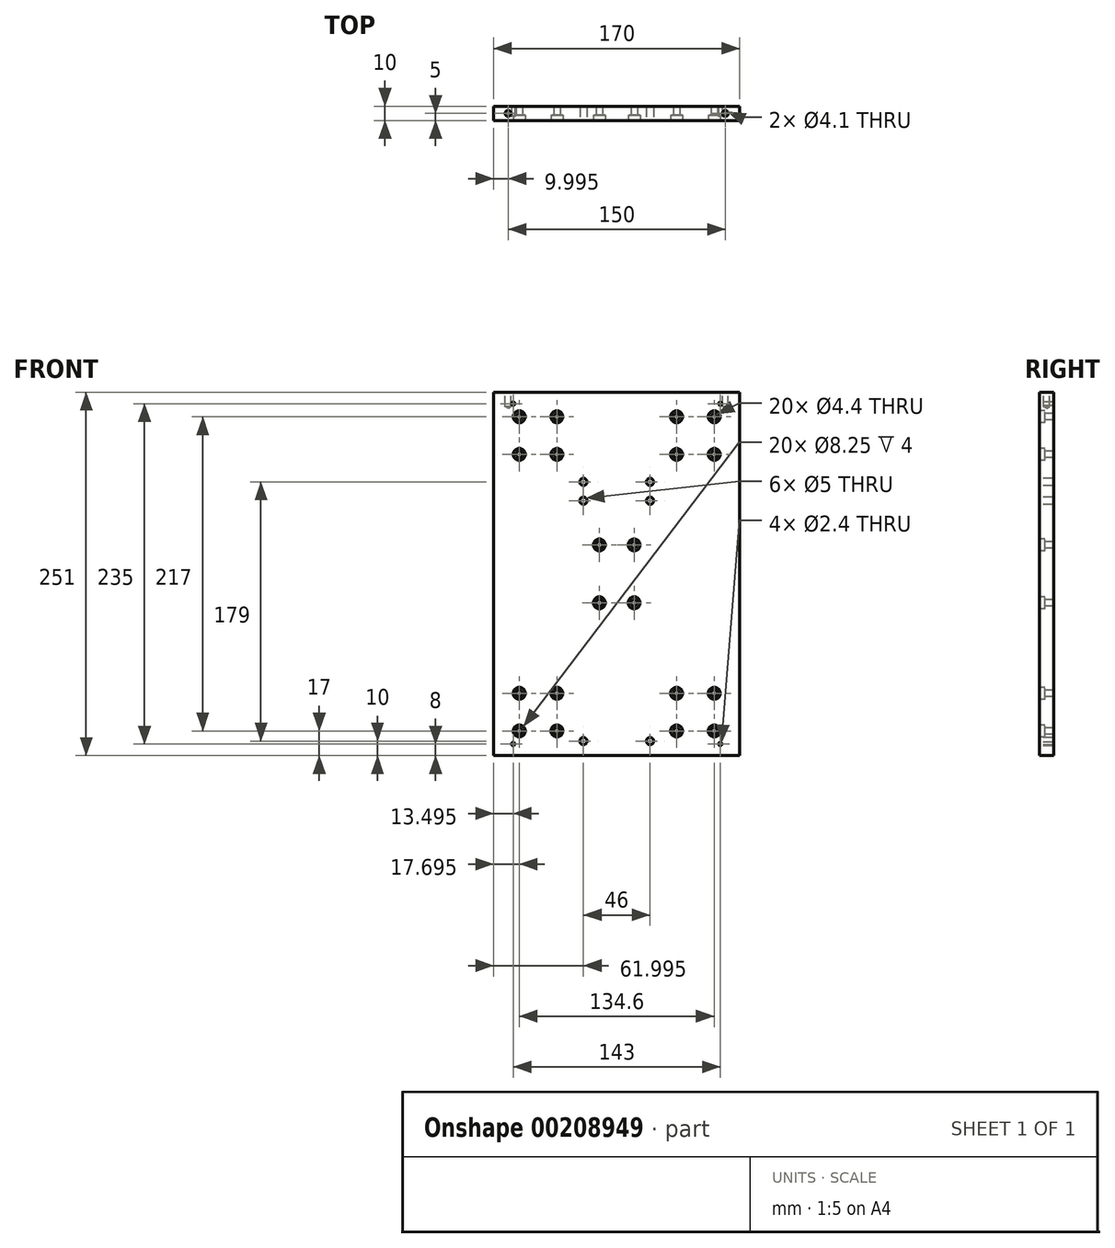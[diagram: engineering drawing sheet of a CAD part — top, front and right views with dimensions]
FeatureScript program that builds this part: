
annotation { "Feature Type Name" : "Feature", "Feature Type Description" : "" }
export const myFeature = defineFeature(function(context is Context, id is Id, definition is map)
    precondition{}
    {
        {
            var Q0;
            Q0=qCreatedBy(makeId("Front.planeOp"),FACE);
            var sketch = newSketch(context, id + "F0", { "sketchPlane" : qUnion([Q0])});
            skLineSegment(sketch, "E0.bottom", {"start": v(-43.58, 205.06) * mm, "end": v(126.42, 205.06) * mm});
            skLineSegment(sketch, "E0.top", {"start": v(-43.58, -40.94) * mm, "end": v(126.42, -40.94) * mm});
            skLineSegment(sketch, "E0.left", {"start": v(-43.58, 205.06) * mm, "end": v(-43.58, -40.94) * mm});
            skLineSegment(sketch, "E0.right", {"start": v(126.42, 205.06) * mm, "end": v(126.42, -40.94) * mm});
            skSolve(sketch);
        }
        {
            var Q0;
            Q0=makeQuery(id+"F0.imprint","IMPRINT",FACE,{"disambiguationData":[TD([[makeQuery(id+"F0.imprint","IMPRINT",EDGE,{"derivedFrom":sQuery(id+"F0.wireOp",EDGE,"E0.bottom")}),-1.0]])]});
            extrude(context, id + "F1", {"entities" : qUnion([Q0]), "depth" : 10 * mm});
        }
        {
            var Q0;
            Q0=makeQuery(id+"F1.opExtrude","CAP_FACE",FACE,{"disambiguationData":[OSD([sQuery(id+"F0.wireOp",EDGE,"E0.bottom"),sQuery(id+"F0.wireOp",EDGE,"E0.top"),sQuery(id+"F0.wireOp",EDGE,"E0.left"),sQuery(id+"F0.wireOp",EDGE,"E0.right")])],"isStart":false});
            var sketch = newSketch(context, id + "F2", { "sketchPlane" : qUnion([Q0])});
            skLineSegment(sketch, "E1", {"start": v(41.42, 205.06) * mm, "end": v(41.42, -40.94) * mm, "construction": true});
            skLineSegment(sketch, "E2", {"start": v(-30.08, 205.06) * mm, "end": v(-30.08, -40.94) * mm, "construction": true});
            skLineSegment(sketch, "E3.MirrorCS", {"start": v(112.92, 205.06) * mm, "end": v(112.92, -40.94) * mm, "construction": true});
            skLineSegment(sketch, "E4", {"start": v(112.92, 202.06) * mm, "end": v(-30.08, 202.06) * mm, "construction": true});
            skLineSegment(sketch, "E5", {"start": v(112.92, -32.94) * mm, "end": v(-30.08, -32.94) * mm, "construction": true});
            skPoint(sketch, "E6", {"position": v(112.92, 202.06) * mm});
            skPoint(sketch, "E7", {"position": v(-30.08, 202.06) * mm});
            skPoint(sketch, "E8", {"position": v(112.92, -32.94) * mm});
            skPoint(sketch, "E9", {"position": v(-30.08, -32.94) * mm});
            skPoint(sketch, "E10", {"position": v(18.42, -30.94) * mm});
            skPoint(sketch, "E11.MirrorP", {"position": v(64.42, -30.94) * mm});
            skLineSegment(sketch, "E12", {"start": v(112.92, 148.06) * mm, "end": v(-30.08, 148.06) * mm, "construction": true});
            skLineSegment(sketch, "E13", {"start": v(112.92, 135.06) * mm, "end": v(-30.08, 135.06) * mm, "construction": true});
            skPoint(sketch, "E14", {"position": v(64.42, 148.06) * mm});
            skPoint(sketch, "E15.MirrorP", {"position": v(18.42, 148.06) * mm});
            skPoint(sketch, "E16", {"position": v(64.42, 135.06) * mm});
            skPoint(sketch, "E17.MirrorP", {"position": v(18.42, 135.06) * mm});
            skLineSegment(sketch, "E18", {"start": v(41.42, 219.06) * mm, "end": v(11.42, 219.06) * mm, "construction": true});
            skLineSegment(sketch, "E19", {"start": v(11.42, 219.06) * mm, "end": v(11.42, 244.06) * mm, "construction": true});
            skLineSegment(sketch, "E20", {"start": v(11.42, 244.06) * mm, "end": v(41.42, 244.06) * mm, "construction": true});
            skLineSegment(sketch, "E21", {"start": v(-43.58, -10.94) * mm, "end": v(126.42, -10.94) * mm, "construction": true});
            skLineSegment(sketch, "E22", {"start": v(-43.58, 180.06) * mm, "end": v(126.42, 180.06) * mm, "construction": true});
            skPoint(sketch, "E23", {"position": v(-25.88, 2.06) * mm});
            skPoint(sketch, "E24.MirrorP", {"position": v(-25.88, -23.94) * mm});
            skPoint(sketch, "E25.MirrorP", {"position": v(108.72, 2.06) * mm});
            skPoint(sketch, "E26.MirrorP", {"position": v(108.72, -23.94) * mm});
            skPoint(sketch, "E27", {"position": v(0.12, 2.06) * mm});
            skPoint(sketch, "E28.MirrorP", {"position": v(82.72, 2.06) * mm});
            skPoint(sketch, "E29.MirrorP", {"position": v(0.12, -23.94) * mm});
            skPoint(sketch, "E30.MirrorP", {"position": v(82.72, -23.94) * mm});
            skPoint(sketch, "E31", {"position": v(-25.88, 193.06) * mm});
            skPoint(sketch, "E32.MirrorP", {"position": v(108.72, 193.06) * mm});
            skLineSegment(sketch, "E33", {"start": v(-25.88, 193.06) * mm, "end": v(108.72, 193.06) * mm, "construction": true});
            skPoint(sketch, "E34", {"position": v(0.12, 193.06) * mm});
            skPoint(sketch, "E35.MirrorP", {"position": v(82.72, 193.06) * mm});
            skPoint(sketch, "E36.MirrorP", {"position": v(-25.88, 167.06) * mm});
            skPoint(sketch, "E37.MirrorP", {"position": v(0.12, 167.06) * mm});
            skPoint(sketch, "E38.MirrorP", {"position": v(82.72, 167.06) * mm});
            skPoint(sketch, "E39.MirrorP", {"position": v(108.72, 167.06) * mm});
            skLineSegment(sketch, "E40", {"start": v(-10.35, 84.56) * mm, "end": v(93.03, 84.56) * mm, "construction": true});
            skPoint(sketch, "E41", {"position": v(29.42, 104.56) * mm});
            skPoint(sketch, "E42.MirrorP", {"position": v(53.42, 104.56) * mm});
            skPoint(sketch, "E43.MirrorP", {"position": v(53.42, 64.56) * mm});
            skPoint(sketch, "E44.MirrorP", {"position": v(29.42, 64.56) * mm});
            skSolve(sketch);
        }
        {
            var Q0;
            Q0=sQuery(id+"F2.wireOp",VERTEX,"E6");
            var Q1;
            Q1=sQuery(id+"F2.wireOp",VERTEX,"E7");
            var Q2;
            Q2=sQuery(id+"F2.wireOp",VERTEX,"E9");
            var Q3;
            Q3=sQuery(id+"F2.wireOp",VERTEX,"E8");
            var Q4;
            Q4=makeQuery(id+"F1.opExtrude","SWEPT_BODY",BODY,{"disambiguationData":[OSD([sQuery(id+"F0.wireOp",EDGE,"E0.bottom"),sQuery(id+"F0.wireOp",EDGE,"E0.top"),sQuery(id+"F0.wireOp",EDGE,"E0.left"),sQuery(id+"F0.wireOp",EDGE,"E0.right")])]});
            hole(context, id + "F3", {"style" : HoleStyle.SIMPLE, "endStyle" : HoleEndStyle.THROUGH, "standardTappedOrClearance" : lookupTablePath({ "standard" : "ISO", "engagement" : "75%", "pitch" : "0.6 mm", "size" : "M3", "type" : "Tapped" }), "standardBlindInLast" : lookupTablePath({ "standard" : "ISO", "engagement" : "75%", "pitch" : "0.6 mm", "size" : "M3", "type" : "Tapped" }), "holeDiameter" : 2.4 * mm, "locations" : qUnion([Q0, Q1, Q2, Q3]), "scope" : qUnion([Q4]), "isTappedThrough" : true, "showTappedDepth" : true});
        }
        {
            var Q0;
            Q0=sQuery(id+"F2.wireOp",VERTEX,"E15.MirrorP");
            var Q1;
            Q1=sQuery(id+"F2.wireOp",VERTEX,"E14");
            var Q2;
            Q2=sQuery(id+"F2.wireOp",VERTEX,"E16");
            var Q3;
            Q3=sQuery(id+"F2.wireOp",VERTEX,"E17.MirrorP");
            var Q4;
            Q4=sQuery(id+"F2.wireOp",VERTEX,"E10");
            var Q5;
            Q5=sQuery(id+"F2.wireOp",VERTEX,"E11.MirrorP");
            var Q6;
            Q6=makeQuery(id+"F1.opExtrude","SWEPT_BODY",BODY,{"disambiguationData":[OSD([sQuery(id+"F0.wireOp",EDGE,"E0.bottom"),sQuery(id+"F0.wireOp",EDGE,"E0.top"),sQuery(id+"F0.wireOp",EDGE,"E0.left"),sQuery(id+"F0.wireOp",EDGE,"E0.right")])]});
            hole(context, id + "F4", {"style" : HoleStyle.SIMPLE, "endStyle" : HoleEndStyle.THROUGH, "standardTappedOrClearance" : lookupTablePath({ "standard" : "ISO", "engagement" : "75%", "pitch" : "1 mm", "size" : "M6", "type" : "Tapped" }), "standardBlindInLast" : lookupTablePath({ "standard" : "ISO", "engagement" : "75%", "pitch" : "1 mm", "size" : "M6", "type" : "Tapped" }), "holeDiameter" : 5 * mm, "locations" : qUnion([Q0, Q1, Q2, Q3, Q4, Q5]), "scope" : qUnion([Q6]), "isTappedThrough" : true, "majorDiameter" : 6 * mm, "showTappedDepth" : true});
        }
        {
            var Q0;
            Q0=makeQuery(id+"F1.opExtrude","SWEPT_FACE",FACE,{"disambiguationData":[OSD([sQuery(id+"F0.wireOp",EDGE,"E0.bottom")])]});
            extrude(context, id + "F5", {"entities" : qUnion([Q0]), "operationType" : NewBodyOperationType.ADD, "depth" : 5 * mm});
        }
        {
            var Q0;
            Q0=sQuery(id+"F2.wireOp",VERTEX,"E24.MirrorP");
            var Q1;
            Q1=sQuery(id+"F2.wireOp",VERTEX,"E23");
            var Q2;
            Q2=sQuery(id+"F2.wireOp",VERTEX,"E27");
            var Q3;
            Q3=sQuery(id+"F2.wireOp",VERTEX,"E29.MirrorP");
            var Q4;
            Q4=sQuery(id+"F2.wireOp",VERTEX,"E30.MirrorP");
            var Q5;
            Q5=sQuery(id+"F2.wireOp",VERTEX,"E28.MirrorP");
            var Q6;
            Q6=sQuery(id+"F2.wireOp",VERTEX,"E25.MirrorP");
            var Q7;
            Q7=sQuery(id+"F2.wireOp",VERTEX,"E26.MirrorP");
            var Q8;
            Q8=sQuery(id+"F2.wireOp",VERTEX,"E31");
            var Q9;
            Q9=sQuery(id+"F2.wireOp",VERTEX,"E36.MirrorP");
            var Q10;
            Q10=sQuery(id+"F2.wireOp",VERTEX,"E37.MirrorP");
            var Q11;
            Q11=sQuery(id+"F2.wireOp",VERTEX,"E34");
            var Q12;
            Q12=sQuery(id+"F2.wireOp",VERTEX,"E35.MirrorP");
            var Q13;
            Q13=sQuery(id+"F2.wireOp",VERTEX,"E32.MirrorP");
            var Q14;
            Q14=sQuery(id+"F2.wireOp",VERTEX,"E39.MirrorP");
            var Q15;
            Q15=sQuery(id+"F2.wireOp",VERTEX,"E38.MirrorP");
            var Q16;
            Q16=makeQuery(id+"F1.opExtrude","SWEPT_BODY",BODY,{"disambiguationData":[OSD([sQuery(id+"F0.wireOp",EDGE,"E0.bottom"),sQuery(id+"F0.wireOp",EDGE,"E0.top"),sQuery(id+"F0.wireOp",EDGE,"E0.left"),sQuery(id+"F0.wireOp",EDGE,"E0.right")])]});
            hole(context, id + "F6", {"style" : HoleStyle.C_BORE, "endStyle" : HoleEndStyle.THROUGH, "standardTappedOrClearance" : lookupTablePath({ "standard" : "ISO", "fit" : "Normal", "size" : "M4", "type" : "Clearance" }), "standardBlindInLast" : lookupTablePath({ "fit" : "Standard", "standard" : "ISO", "size" : "M4", "type" : "Clearance" }), "holeDiameter" : 4.4 * mm, "cBoreDiameter" : 8.25 * mm, "cBoreDepth" : 4 * mm, "locations" : qUnion([Q0, Q1, Q2, Q3, Q4, Q5, Q6, Q7, Q8, Q9, Q10, Q11, Q12, Q13, Q14, Q15]), "scope" : qUnion([Q16]), "isTappedThrough" : true});
        }
        {
            var Q0;
            Q0=makeQuery(id+"F5.opExtrude","CAP_FACE",FACE,{"disambiguationData":[OSD([sQuery(id+"F0.wireOp",EDGE,"E0.bottom")])],"isStart":false});
            var sketch = newSketch(context, id + "F7", { "sketchPlane" : qUnion([Q0])});
            skLineSegment(sketch, "E45", {"start": v(126.42, -5) * mm, "end": v(-43.58, -5) * mm, "construction": true});
            skPoint(sketch, "E46", {"position": v(116.42, -5) * mm});
            skPoint(sketch, "E47", {"position": v(-33.58, -5) * mm});
            skSolve(sketch);
        }
        {
            var Q0;
            Q0=sQuery(id+"F7.wireOp",VERTEX,"E47");
            var Q1;
            Q1=sQuery(id+"F7.wireOp",VERTEX,"E46");
            var Q2;
            Q2=makeQuery(id+"F1.opExtrude","SWEPT_BODY",BODY,{"disambiguationData":[OSD([sQuery(id+"F0.wireOp",EDGE,"E0.bottom"),sQuery(id+"F0.wireOp",EDGE,"E0.top"),sQuery(id+"F0.wireOp",EDGE,"E0.left"),sQuery(id+"F0.wireOp",EDGE,"E0.right")])]});
            hole(context, id + "F8", {"style" : HoleStyle.SIMPLE, "endStyle" : HoleEndStyle.BLIND, "standardTappedOrClearance" : lookupTablePath({ "standard" : "ISO", "engagement" : "75%", "pitch" : "0.9 mm", "size" : "M5", "type" : "Tapped" }), "standardBlindInLast" : lookupTablePath({ "standard" : "ISO", "engagement" : "75%", "pitch" : "0.9 mm", "size" : "M5", "type" : "Tapped" }), "holeDiameter" : 4.1 * mm, "holeDepth" : 10 * mm, "locations" : qUnion([Q0, Q1]), "scope" : qUnion([Q2])});
        }
        {
            var Q0;
            Q0=sQuery(id+"F2.wireOp",VERTEX,"E41");
            var Q1;
            Q1=sQuery(id+"F2.wireOp",VERTEX,"E42.MirrorP");
            var Q2;
            Q2=sQuery(id+"F2.wireOp",VERTEX,"E43.MirrorP");
            var Q3;
            Q3=sQuery(id+"F2.wireOp",VERTEX,"E44.MirrorP");
            var Q4;
            Q4=makeQuery(id+"F1.opExtrude","SWEPT_BODY",BODY,{"disambiguationData":[OSD([sQuery(id+"F0.wireOp",EDGE,"E0.bottom"),sQuery(id+"F0.wireOp",EDGE,"E0.top"),sQuery(id+"F0.wireOp",EDGE,"E0.left"),sQuery(id+"F0.wireOp",EDGE,"E0.right")])]});
            hole(context, id + "F9", {"style" : HoleStyle.C_BORE, "endStyle" : HoleEndStyle.THROUGH, "standardTappedOrClearance" : lookupTablePath({ "standard" : "ISO", "fit" : "Normal", "size" : "M4", "type" : "Clearance" }), "standardBlindInLast" : lookupTablePath({ "fit" : "Standard", "standard" : "ISO", "size" : "M4", "type" : "Clearance" }), "holeDiameter" : 4.4 * mm, "cBoreDiameter" : 8.25 * mm, "cBoreDepth" : 4 * mm, "locations" : qUnion([Q0, Q1, Q2, Q3]), "scope" : qUnion([Q4]), "isTappedThrough" : true});
        }
    });
